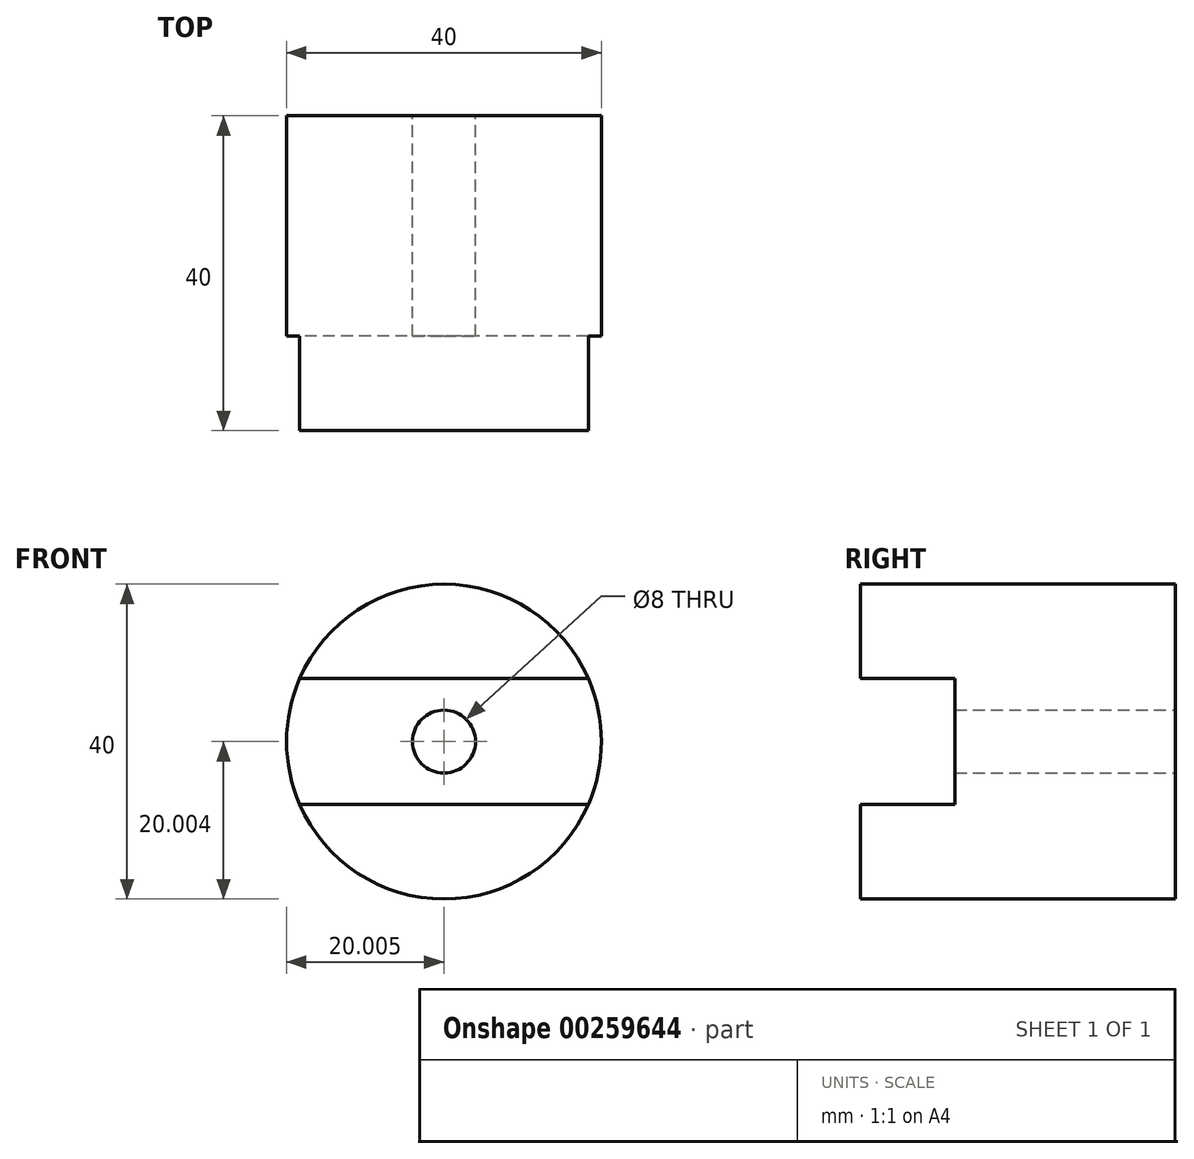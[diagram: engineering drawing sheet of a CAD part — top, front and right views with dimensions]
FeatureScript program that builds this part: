
annotation { "Feature Type Name" : "Feature", "Feature Type Description" : "" }
export const myFeature = defineFeature(function(context is Context, id is Id, definition is map)
    precondition{}
    {
        {
            var Q0;
            Q0=qCreatedBy(makeId("Front.planeOp"),FACE);
            var sketch = newSketch(context, id + "F0", { "sketchPlane" : qUnion([Q0])});
            skCircle(sketch, "E0", {"center": v(-51.9, 45.8) * mm, "radius": 20 * mm});
            skCircle(sketch, "E1", {"center": v(-51.9, 45.8) * mm, "radius": 4 * mm});
            skLineSegment(sketch, "E2.bottom", {"start": v(-33.57, 37.8) * mm, "end": v(-70.24, 37.8) * mm});
            skLineSegment(sketch, "E2.top", {"start": v(-33.57, 53.8) * mm, "end": v(-70.24, 53.8) * mm});
            skPoint(sketch, "E3", {"position": v(-70.24, 37.8) * mm});
            skPoint(sketch, "E4", {"position": v(-70.24, 53.8) * mm});
            skPoint(sketch, "E5", {"position": v(-33.57, 53.8) * mm});
            skPoint(sketch, "E6", {"position": v(-33.57, 37.8) * mm});
            skPoint(sketch, "E2.right.start.orphan", {"position": v(-72.4, 37.8) * mm});
            skPoint(sketch, "E7.orphan", {"position": v(-72.4, 53.8) * mm});
            skPoint(sketch, "E2.left.end.orphan", {"position": v(-31.4, 53.8) * mm});
            skPoint(sketch, "E2.left.start.orphan", {"position": v(-31.4, 37.8) * mm});
            skSolve(sketch);
        }
        {
            var Q0;
            {var subQ0=sQuery(id+"F0.wireOp",EDGE,"E2.top");Q0=makeQuery(id+"F0.imprint","IMPRINT",FACE,{"disambiguationData":[TD([[makeQuery(id+"F0.imprint","IMPRINT",EDGE,{"derivedFrom":subQ0}),-1.0]])]});}
            var Q1;
            {var subQ0=sQuery(id+"F0.wireOp",EDGE,"E2.bottom");Q1=makeQuery(id+"F0.imprint","IMPRINT",FACE,{"disambiguationData":[TD([[makeQuery(id+"F0.imprint","IMPRINT",EDGE,{"derivedFrom":subQ0}),1.0]])]});}
            extrude(context, id + "F1", {"entities" : qUnion([Q0, Q1]), "depth" : 40 * mm});
        }
        {
            var Q0;
            Q0 = qSketchRegion(id + "F0", true);
            extrude(context, id + "F2", {"entities" : qUnion([Q0]), "operationType" : NewBodyOperationType.ADD, "depth" : 28 * mm});
        }
    });
